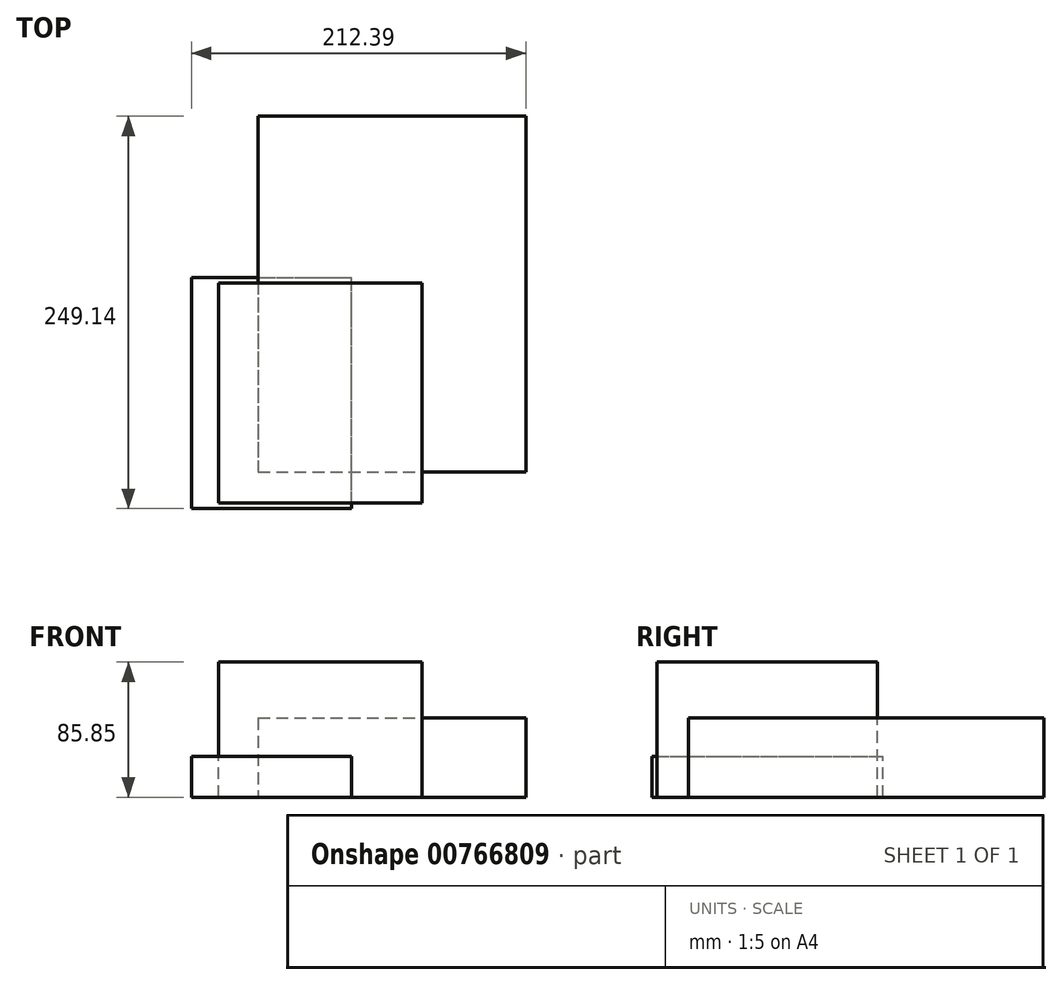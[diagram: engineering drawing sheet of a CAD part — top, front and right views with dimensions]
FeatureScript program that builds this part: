
annotation { "Feature Type Name" : "Feature", "Feature Type Description" : "" }
export const myFeature = defineFeature(function(context is Context, id is Id, definition is map)
    precondition{}
    {
        {
            var Q0;
            Q0=qCreatedBy(makeId("Front.planeOp"),FACE);
            var sketch = newSketch(context, id + "F0", { "sketchPlane" : qUnion([Q0])});
            skLineSegment(sketch, "E0.bottom", {"start": v(-42.46, 0) * mm, "end": v(59.4, 0) * mm});
            skLineSegment(sketch, "E0.top", {"start": v(-42.46, 25.9) * mm, "end": v(59.4, 25.9) * mm});
            skLineSegment(sketch, "E0.left", {"start": v(-42.46, 0) * mm, "end": v(-42.46, 25.9) * mm});
            skLineSegment(sketch, "E0.right", {"start": v(59.4, 0) * mm, "end": v(59.4, 25.9) * mm});
            skSolve(sketch);
        }
        {
            var Q0;
            Q0=makeQuery(id+"F0.imprint","IMPRINT",FACE,{"disambiguationData":[TD([[makeQuery(id+"F0.imprint","IMPRINT",EDGE,{"derivedFrom":sQuery(id+"F0.wireOp",EDGE,"E0.bottom")}),1.0]])]});
            extrude(context, id + "F1", {"entities" : qUnion([Q0]), "endBound" : BoundingType.SYMMETRIC, "depth" : 146.8 * mm, "offsetDistance" : 25.4 * mm});
        }
        {
            var Q0;
            Q0=qCreatedBy(makeId("Front.planeOp"),FACE);
            var sketch = newSketch(context, id + "F2", { "sketchPlane" : qUnion([Q0])});
            skLineSegment(sketch, "E1.bottom", {"start": v(-25.24, 0) * mm, "end": v(104.04, 0) * mm});
            skLineSegment(sketch, "E1.top", {"start": v(-25.24, 85.85) * mm, "end": v(104.04, 85.85) * mm});
            skLineSegment(sketch, "E1.left", {"start": v(-25.24, 0) * mm, "end": v(-25.24, 85.85) * mm});
            skLineSegment(sketch, "E1.right", {"start": v(104.04, 0) * mm, "end": v(104.04, 85.85) * mm});
            skSolve(sketch);
        }
        {
            var Q0;
            Q0=makeQuery(id+"F2.imprint","IMPRINT",FACE,{"disambiguationData":[TD([[makeQuery(id+"F2.imprint","IMPRINT",EDGE,{"derivedFrom":sQuery(id+"F2.wireOp",EDGE,"E1.bottom")}),1.0]])]});
            extrude(context, id + "F3", {"entities" : qUnion([Q0]), "endBound" : BoundingType.SYMMETRIC, "depth" : 139.95 * mm, "offsetDistance" : 25.4 * mm});
        }
        {
            var Q0;
            Q0=qCreatedBy(makeId("Top.planeOp"),FACE);
            var sketch = newSketch(context, id + "F4", { "sketchPlane" : qUnion([Q0])});
            skLineSegment(sketch, "E2.bottom", {"start": v(0, 175.73) * mm, "end": v(169.93, 175.73) * mm});
            skLineSegment(sketch, "E2.top", {"start": v(0, -50.08) * mm, "end": v(169.93, -50.08) * mm});
            skLineSegment(sketch, "E2.left", {"start": v(0, 175.73) * mm, "end": v(0, -50.08) * mm});
            skLineSegment(sketch, "E2.right", {"start": v(169.93, 175.73) * mm, "end": v(169.93, -50.08) * mm});
            skSolve(sketch);
        }
        {
            var Q0;
            Q0 = qSketchRegion(id + "F4", true);
            extrude(context, id + "F5", {"entities" : qUnion([Q0]), "depth" : 50.3 * mm, "offsetDistance" : 25.4 * mm});
        }
    });
